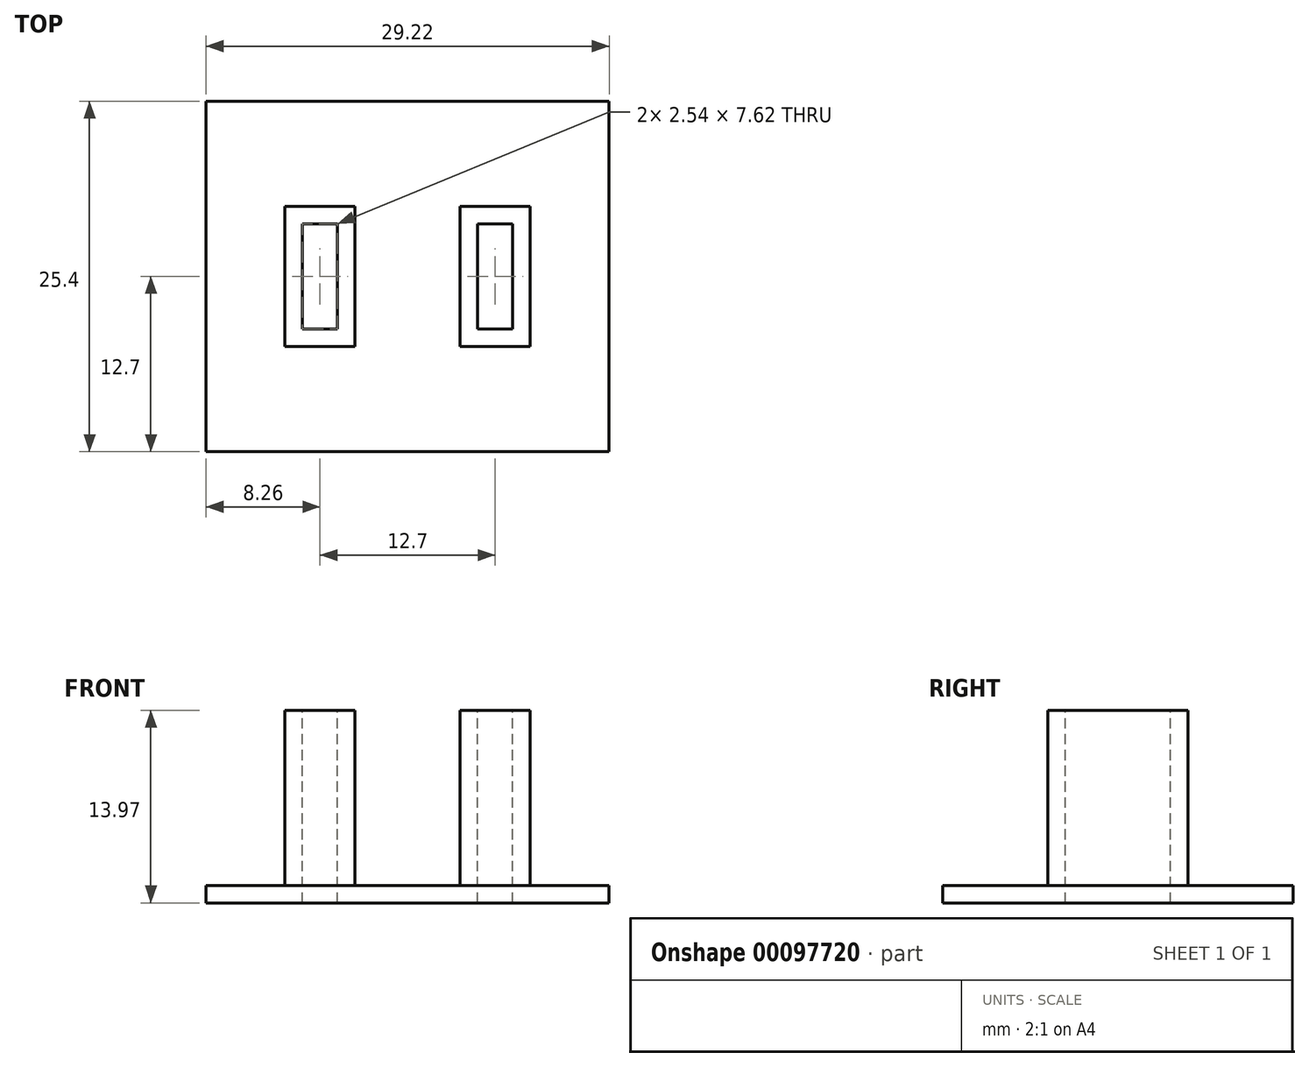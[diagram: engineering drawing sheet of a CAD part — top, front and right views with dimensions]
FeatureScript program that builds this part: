
annotation { "Feature Type Name" : "Feature", "Feature Type Description" : "" }
export const myFeature = defineFeature(function(context is Context, id is Id, definition is map)
    precondition{}
    {
        {
            var Q0;
            Q0=qCreatedBy(makeId("Top.planeOp"),FACE);
            var sketch = newSketch(context, id + "F0", { "sketchPlane" : qUnion([Q0])});
            skLineSegment(sketch, "E0.bottom", {"start": v(6.35, -7.78) * mm, "end": v(-6.35, -7.78) * mm});
            skLineSegment(sketch, "E0.top", {"start": v(6.35, 7.78) * mm, "end": v(-6.35, 7.78) * mm});
            skLineSegment(sketch, "E0.left", {"start": v(6.35, -7.78) * mm, "end": v(6.35, 7.78) * mm});
            skLineSegment(sketch, "E0.right", {"start": v(-6.35, -7.78) * mm, "end": v(-6.35, 7.78) * mm});
            skPoint(sketch, "E0.middle", {"position": v(0, 0) * mm});
            skLineSegment(sketch, "E1.bottom", {"start": v(-7.62, -3.8) * mm, "end": v(-5.08, -3.8) * mm});
            skLineSegment(sketch, "E1.top", {"start": v(-7.62, 3.81) * mm, "end": v(-5.08, 3.81) * mm});
            skLineSegment(sketch, "E1.left", {"start": v(-7.62, -3.8) * mm, "end": v(-7.62, 3.81) * mm});
            skLineSegment(sketch, "E1.right", {"start": v(-5.08, -3.81) * mm, "end": v(-5.08, 3.81) * mm});
            skPoint(sketch, "E1.middle", {"position": v(-6.35, 0) * mm});
            skLineSegment(sketch, "E2.bottom", {"start": v(7.62, -3.81) * mm, "end": v(5.08, -3.81) * mm});
            skLineSegment(sketch, "E2.top", {"start": v(7.62, 3.8) * mm, "end": v(5.08, 3.8) * mm});
            skLineSegment(sketch, "E2.left", {"start": v(7.62, -3.81) * mm, "end": v(7.62, 3.81) * mm});
            skLineSegment(sketch, "E2.right", {"start": v(5.08, -3.81) * mm, "end": v(5.08, 3.81) * mm});
            skPoint(sketch, "E2.middle", {"position": v(6.35, 0) * mm});
            skLineSegment(sketch, "E3.0", {"start": v(-3.81, -5.08) * mm, "end": v(-3.81, 5.08) * mm});
            skLineSegment(sketch, "E3.1", {"start": v(-8.9, -5.08) * mm, "end": v(-3.81, -5.08) * mm});
            skLineSegment(sketch, "E3.2", {"start": v(-8.9, -5.08) * mm, "end": v(-8.9, 5.08) * mm});
            skLineSegment(sketch, "E3.3", {"start": v(-8.9, 5.08) * mm, "end": v(-3.81, 5.08) * mm});
            skLineSegment(sketch, "E4", {"start": v(0, -7.78) * mm, "end": v(0, 7.78) * mm});
            skLineSegment(sketch, "E5.MirrorCS", {"start": v(8.9, -5.08) * mm, "end": v(3.81, -5.08) * mm});
            skLineSegment(sketch, "E6.MirrorCS", {"start": v(3.81, -5.08) * mm, "end": v(3.81, 5.08) * mm});
            skLineSegment(sketch, "E7.MirrorCS", {"start": v(8.9, 5.08) * mm, "end": v(3.81, 5.08) * mm});
            skLineSegment(sketch, "E8.MirrorCS", {"start": v(8.9, -5.08) * mm, "end": v(8.9, 5.08) * mm});
            skLineSegment(sketch, "E9.bottom", {"start": v(14.6, -12.7) * mm, "end": v(-14.6, -12.7) * mm});
            skLineSegment(sketch, "E9.top", {"start": v(14.6, 12.7) * mm, "end": v(-14.6, 12.7) * mm});
            skLineSegment(sketch, "E9.left", {"start": v(14.6, -12.7) * mm, "end": v(14.6, 12.7) * mm});
            skLineSegment(sketch, "E9.right", {"start": v(-14.6, -12.7) * mm, "end": v(-14.6, 12.7) * mm});
            skSolve(sketch);
        }
        {
            var Q0;
            {var subQ11=sQuery(id+"F0.wireOp",EDGE,"E3.2");Q0=makeQuery(id+"F0.imprint","IMPRINT",FACE,{"disambiguationData":[TD([[makeQuery(id+"F0.imprint","IMPRINT",EDGE,{"derivedFrom":subQ11}),1.0]])]});}
            var Q1;
            {var subQ5=sQuery(id+"F0.wireOp",EDGE,"E3.0");Q1=makeQuery(id+"F0.imprint","IMPRINT",FACE,{"disambiguationData":[TD([[makeQuery(id+"F0.imprint","IMPRINT",EDGE,{"derivedFrom":subQ5}),-1.0]])]});}
            var Q2;
            {var subQ5=sQuery(id+"F0.wireOp",EDGE,"E4");Q2=makeQuery(id+"F0.imprint","IMPRINT",FACE,{"disambiguationData":[TD([[makeQuery(id+"F0.imprint","IMPRINT",EDGE,{"derivedFrom":subQ5}),-1.0]])]});}
            var Q3;
            {var subQ0=sQuery(id+"F0.wireOp",EDGE,"E1.left");Q3=makeQuery(id+"F0.imprint","IMPRINT",FACE,{"disambiguationData":[TD([[makeQuery(id+"F0.imprint","IMPRINT",EDGE,{"derivedFrom":subQ0}),1.0]])]});}
            var Q4;
            {var subQ0=sQuery(id+"F0.wireOp",EDGE,"E1.right");Q4=makeQuery(id+"F0.imprint","IMPRINT",FACE,{"disambiguationData":[TD([[makeQuery(id+"F0.imprint","IMPRINT",EDGE,{"derivedFrom":subQ0}),-1.0]])]});}
            var Q5;
            {var subQ0=sQuery(id+"F0.wireOp",EDGE,"E2.right");Q5=makeQuery(id+"F0.imprint","IMPRINT",FACE,{"disambiguationData":[TD([[makeQuery(id+"F0.imprint","IMPRINT",EDGE,{"derivedFrom":subQ0}),1.0]])]});}
            var Q6;
            {var subQ0=sQuery(id+"F0.wireOp",EDGE,"E2.left");Q6=makeQuery(id+"F0.imprint","IMPRINT",FACE,{"disambiguationData":[TD([[makeQuery(id+"F0.imprint","IMPRINT",EDGE,{"derivedFrom":subQ0}),-1.0]])]});}
            extrude(context, id + "F1", {"entities" : qUnion([Q0, Q1, Q2, Q3, Q4, Q5, Q6]), "oppositeDirection" : true, "depth" : 1.27 * mm});
        }
        {
            var Q0;
            {var subQ0=sQuery(id+"F0.wireOp",EDGE,"E2.left");Q0=makeQuery(id+"F0.imprint","IMPRINT",FACE,{"disambiguationData":[TD([[makeQuery(id+"F0.imprint","IMPRINT",EDGE,{"derivedFrom":subQ0}),-1.0]])]});}
            var Q1;
            {var subQ0=sQuery(id+"F0.wireOp",EDGE,"E2.right");Q1=makeQuery(id+"F0.imprint","IMPRINT",FACE,{"disambiguationData":[TD([[makeQuery(id+"F0.imprint","IMPRINT",EDGE,{"derivedFrom":subQ0}),1.0]])]});}
            var Q2;
            {var subQ0=sQuery(id+"F0.wireOp",EDGE,"E1.right");Q2=makeQuery(id+"F0.imprint","IMPRINT",FACE,{"disambiguationData":[TD([[makeQuery(id+"F0.imprint","IMPRINT",EDGE,{"derivedFrom":subQ0}),-1.0]])]});}
            var Q3;
            {var subQ0=sQuery(id+"F0.wireOp",EDGE,"E1.left");Q3=makeQuery(id+"F0.imprint","IMPRINT",FACE,{"disambiguationData":[TD([[makeQuery(id+"F0.imprint","IMPRINT",EDGE,{"derivedFrom":subQ0}),1.0]])]});}
            extrude(context, id + "F2", {"entities" : qUnion([Q0, Q1, Q2, Q3]), "operationType" : NewBodyOperationType.ADD, "depth" : 12.7 * mm});
        }
    });
